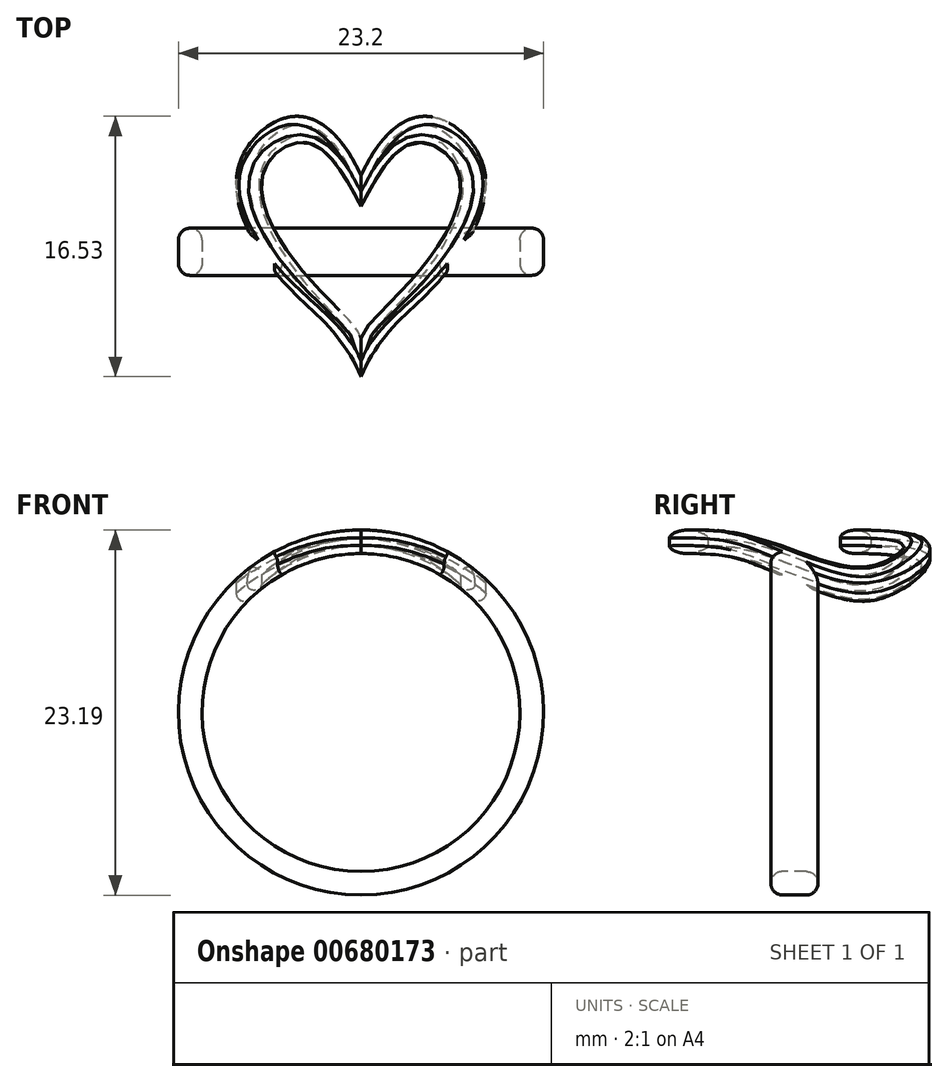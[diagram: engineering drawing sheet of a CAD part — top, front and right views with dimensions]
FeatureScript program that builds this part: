
annotation { "Feature Type Name" : "Feature", "Feature Type Description" : "" }
export const myFeature = defineFeature(function(context is Context, id is Id, definition is map)
    precondition{}
    {
        {
            var Q0;
            Q0=qCreatedBy(makeId("Top.planeOp"),FACE);
            var sketch = newSketch(context, id + "F0", { "sketchPlane" : qUnion([Q0])});
            skFitSpline(sketch, "E0", {"points": [v(0, 4.84) * mm, v(-4.43, 8.58) * mm, v(-7.87, 5.02) * mm, v(-5.4, -1.36) * mm, v(-1.9, -4.93) * mm, v(0, -7.93) * mm], "startDerivative": vector(-17.19, 37.33) * mm, "endDerivative": vector(6.53, -16.13) * mm});
            skFitSpline(sketch, "E1.MirrorCS", {"points": [v(0, 4.84) * mm, v(4.43, 8.58) * mm, v(7.87, 5.02) * mm, v(5.4, -1.36) * mm, v(1.9, -4.93) * mm, v(0, -7.93) * mm], "startDerivative": vector(17.19, 37.33) * mm, "endDerivative": vector(-6.53, -16.13) * mm});
            skSolve(sketch);
        }
        {
            var Q0;
            Q0 = qSketchRegion(id + "F0", true);
            extrude(context, id + "F1", {"entities" : qUnion([Q0]), "depth" : 19.05 * mm, "offsetDistance" : 25.4 * mm});
        }
        {
            var Q0;
            Q0=qCreatedBy(makeId("Front.planeOp"),FACE);
            var sketch = newSketch(context, id + "F2", { "sketchPlane" : qUnion([Q0])});
            skCircle(sketch, "E2", {"center": v(0, 0) * mm, "radius": 10.1 * mm});
            skCircle(sketch, "E3", {"center": v(0, 0) * mm, "radius": 11.6 * mm});
            skCircle(sketch, "E4", {"center": v(0, 0) * mm, "radius": 13.1 * mm});
            skCircle(sketch, "E5", {"center": v(0, 0) * mm, "radius": 23.1 * mm});
            skSolve(sketch);
        }
        {
            var Q0;
            Q0=makeQuery(id+"F2.imprint","IMPRINT",FACE,{"disambiguationData":[TD([[makeQuery(id+"F2.imprint","IMPRINT",EDGE,{"derivedFrom":sQuery(id+"F2.wireOp",EDGE,"E2")}),1.0]])]});
            extrude(context, id + "F3", {"entities" : qUnion([Q0]), "operationType" : NewBodyOperationType.REMOVE, "endBound" : BoundingType.SYMMETRIC, "oppositeDirection" : true, "depth" : 25.4 * mm, "offsetDistance" : 25.4 * mm});
        }
        {
            var Q0;
            Q0=makeQuery(id+"F2.imprint","IMPRINT",FACE,{"disambiguationData":[TD([[makeQuery(id+"F2.imprint","IMPRINT",EDGE,{"derivedFrom":sQuery(id+"F2.wireOp",EDGE,"E4")}),-1.0]])]});
            var Q1;
            Q1=makeQuery(id+"F2.imprint","IMPRINT",FACE,{"disambiguationData":[TD([[makeQuery(id+"F2.imprint","IMPRINT",EDGE,{"derivedFrom":sQuery(id+"F2.wireOp",EDGE,"E3")}),-1.0]])]});
            extrude(context, id + "F4", {"entities" : qUnion([Q0, Q1]), "operationType" : NewBodyOperationType.REMOVE, "endBound" : BoundingType.SYMMETRIC, "oppositeDirection" : true, "depth" : 25.4 * mm, "offsetDistance" : 25.4 * mm});
        }
        {
            var Q0;
            Q0=makeQuery(id+"F2.imprint","IMPRINT",FACE,{"disambiguationData":[TD([[makeQuery(id+"F2.imprint","IMPRINT",EDGE,{"derivedFrom":sQuery(id+"F2.wireOp",EDGE,"E2")}),-1.0]])]});
            extrude(context, id + "F5", {"entities" : qUnion([Q0]), "operationType" : NewBodyOperationType.ADD, "endBound" : BoundingType.SYMMETRIC, "oppositeDirection" : true, "depth" : 3 * mm, "offsetDistance" : 25.4 * mm});
        }
        {
            var Q0;
            Q0=qCreatedBy(makeId("Top.planeOp"),FACE);
            var sketch = newSketch(context, id + "F6", { "sketchPlane" : qUnion([Q0])});
            skFitSpline(sketch, "E6", {"points": [v(0, 2.9) * mm, v(-3.3, 6.9) * mm, v(-6.2, 5) * mm, v(-4.18, -0.63) * mm, v(-0.65, -4.45) * mm, v(0, -5.5) * mm], "startDerivative": vector(-11.42, 20.67) * mm, "endDerivative": vector(3.06, -10.59) * mm});
            skFitSpline(sketch, "E7.MirrorCS", {"points": [v(0, 2.9) * mm, v(3.3, 6.9) * mm, v(6.2, 5) * mm, v(4.18, -0.63) * mm, v(0.65, -4.45) * mm, v(0, -5.5) * mm], "startDerivative": vector(11.42, 20.67) * mm, "endDerivative": vector(-3.06, -10.59) * mm});
            skSolve(sketch);
        }
        {
            var Q0;
            Q0 = qSketchRegion(id + "F6", true);
            extrude(context, id + "F7", {"entities" : qUnion([Q0]), "operationType" : NewBodyOperationType.REMOVE, "depth" : 25.4 * mm, "offsetDistance" : 25.4 * mm});
        }
        {
            var Q0;
            Q0=makeQuery(id+"F5.opExtrude","CAP_EDGE",EDGE,{"disambiguationData":[OSD([sQuery(id+"F2.wireOp",EDGE,"E3")])],"isStart":false});
            var Q1;
            Q1=makeQuery(id+"F5.opExtrude","CAP_EDGE",EDGE,{"disambiguationData":[OSD([sQuery(id+"F2.wireOp",EDGE,"E3")])],"isStart":true});
            var Q2;
            Q2=makeQuery(id+"F5.opExtrude","CAP_EDGE",EDGE,{"disambiguationData":[OSD([sQuery(id+"F2.wireOp",EDGE,"E2")])],"isStart":true});
            var Q3;
            Q3=makeQuery(id+"F5.opExtrude","CAP_EDGE",EDGE,{"disambiguationData":[OSD([sQuery(id+"F2.wireOp",EDGE,"E2")])],"isStart":false});
            fillet(context, id + "F8", {"entities" : qUnion([Q0, Q1, Q2, Q3]), "radius" : 0.75 * mm, "tangentPropagation" : true, "allowEdgeOverflow" : false});
        }
        {
            var Q0;
            {var subQ0=sQuery(id+"F2.wireOp",EDGE,"E2");Q0=makeQuery(id+"F7.boolean.opBoolean","INTERSECT",EDGE,{"derivedFrom":[makeQuery(id+"F5.boolean.opBoolean","MERGE",FACE,{"derivedFrom":[makeQuery(id+"F3.boolean.opBoolean","COPY",FACE,{"derivedFrom":makeQuery(id+"F3.opExtrude","SWEPT_FACE",FACE,{"disambiguationData":[OSD([subQ0])]})}),makeQuery(id+"F5.opExtrude","SWEPT_FACE",FACE,{"disambiguationData":[OSD([subQ0])]})]}),makeQuery(id+"F7.opExtrude","SWEPT_FACE",FACE,{"disambiguationData":[OSD([sQuery(id+"F6.wireOp",EDGE,"E6")])]})]});}
            var Q1;
            {var subQ0=sQuery(id+"F2.wireOp",EDGE,"E3");Q1=makeQuery(id+"F7.boolean.opBoolean","INTERSECT",EDGE,{"derivedFrom":[makeQuery(id+"F5.boolean.opBoolean","MERGE",FACE,{"derivedFrom":[makeQuery(id+"F4.boolean.opBoolean","COPY",FACE,{"derivedFrom":makeQuery(id+"F4.opExtrude","SWEPT_FACE",FACE,{"disambiguationData":[OSD([subQ0])]})}),makeQuery(id+"F5.opExtrude","SWEPT_FACE",FACE,{"disambiguationData":[OSD([subQ0])]})]}),makeQuery(id+"F7.opExtrude","SWEPT_FACE",FACE,{"disambiguationData":[OSD([sQuery(id+"F6.wireOp",EDGE,"E7.MirrorCS")])]})]});}
            var Q2;
            {var subQ0=sQuery(id+"F2.wireOp",EDGE,"E2");Q2=makeQuery(id+"F7.boolean.opBoolean","INTERSECT",EDGE,{"derivedFrom":[makeQuery(id+"F5.boolean.opBoolean","MERGE",FACE,{"derivedFrom":[makeQuery(id+"F3.boolean.opBoolean","COPY",FACE,{"derivedFrom":makeQuery(id+"F3.opExtrude","SWEPT_FACE",FACE,{"disambiguationData":[OSD([subQ0])]})}),makeQuery(id+"F5.opExtrude","SWEPT_FACE",FACE,{"disambiguationData":[OSD([subQ0])]})]}),makeQuery(id+"F7.opExtrude","SWEPT_FACE",FACE,{"disambiguationData":[OSD([sQuery(id+"F6.wireOp",EDGE,"E7.MirrorCS")])]})]});}
            var Q3;
            {var subQ0=sQuery(id+"F2.wireOp",EDGE,"E3");Q3=makeQuery(id+"F7.boolean.opBoolean","INTERSECT",EDGE,{"derivedFrom":[makeQuery(id+"F5.boolean.opBoolean","MERGE",FACE,{"derivedFrom":[makeQuery(id+"F4.boolean.opBoolean","COPY",FACE,{"derivedFrom":makeQuery(id+"F4.opExtrude","SWEPT_FACE",FACE,{"disambiguationData":[OSD([subQ0])]})}),makeQuery(id+"F5.opExtrude","SWEPT_FACE",FACE,{"disambiguationData":[OSD([subQ0])]})]}),makeQuery(id+"F7.opExtrude","SWEPT_FACE",FACE,{"disambiguationData":[OSD([sQuery(id+"F6.wireOp",EDGE,"E6")])]})]});}
            var Q4;
            {var subQ0=sQuery(id+"F2.wireOp",EDGE,"E3");var subQ1=makeQuery(id+"F4.opExtrude","SWEPT_FACE",FACE,{"disambiguationData":[OSD([subQ0])]});var subQ2=makeQuery(id+"F1.opExtrude","SWEPT_FACE",FACE,{"disambiguationData":[OSD([sQuery(id+"F0.wireOp",EDGE,"E0")])]});Q4=makeQuery(id+"F5.boolean.opBoolean","SPLIT",EDGE,{"disambiguationData":[TD([makeQuery(id+"F5.opExtrude","CAP_FACE",FACE,{"disambiguationData":[OSD([sQuery(id+"F2.wireOp",EDGE,"E2"),subQ0])],"isStart":false})])],"derivedFrom":makeQuery(id+"F4.boolean.opBoolean","INTERSECT",EDGE,{"derivedFrom":[subQ2,subQ1]})});}
            var Q5;
            {var subQ0=sQuery(id+"F2.wireOp",EDGE,"E3");var subQ1=makeQuery(id+"F4.opExtrude","SWEPT_FACE",FACE,{"disambiguationData":[OSD([subQ0])]});var subQ2=makeQuery(id+"F1.opExtrude","SWEPT_FACE",FACE,{"disambiguationData":[OSD([sQuery(id+"F0.wireOp",EDGE,"E1.MirrorCS")])]});Q5=makeQuery(id+"F5.boolean.opBoolean","SPLIT",EDGE,{"disambiguationData":[TD([makeQuery(id+"F5.opExtrude","CAP_FACE",FACE,{"disambiguationData":[OSD([sQuery(id+"F2.wireOp",EDGE,"E2"),subQ0])],"isStart":false})])],"derivedFrom":makeQuery(id+"F4.boolean.opBoolean","INTERSECT",EDGE,{"derivedFrom":[subQ2,subQ1]})});}
            var Q6;
            {var subQ0=sQuery(id+"F2.wireOp",EDGE,"E3");var subQ1=makeQuery(id+"F4.opExtrude","SWEPT_FACE",FACE,{"disambiguationData":[OSD([subQ0])]});var subQ2=makeQuery(id+"F1.opExtrude","SWEPT_FACE",FACE,{"disambiguationData":[OSD([sQuery(id+"F0.wireOp",EDGE,"E1.MirrorCS")])]});Q6=makeQuery(id+"F5.boolean.opBoolean","SPLIT",EDGE,{"disambiguationData":[TD([makeQuery(id+"F5.opExtrude","CAP_FACE",FACE,{"disambiguationData":[OSD([sQuery(id+"F2.wireOp",EDGE,"E2"),subQ0])],"isStart":true})])],"derivedFrom":makeQuery(id+"F4.boolean.opBoolean","INTERSECT",EDGE,{"derivedFrom":[subQ2,subQ1]})});}
            var Q7;
            {var subQ0=sQuery(id+"F2.wireOp",EDGE,"E3");var subQ1=makeQuery(id+"F4.opExtrude","SWEPT_FACE",FACE,{"disambiguationData":[OSD([subQ0])]});var subQ2=makeQuery(id+"F1.opExtrude","SWEPT_FACE",FACE,{"disambiguationData":[OSD([sQuery(id+"F0.wireOp",EDGE,"E0")])]});Q7=makeQuery(id+"F5.boolean.opBoolean","SPLIT",EDGE,{"disambiguationData":[TD([makeQuery(id+"F5.opExtrude","CAP_FACE",FACE,{"disambiguationData":[OSD([sQuery(id+"F2.wireOp",EDGE,"E2"),subQ0])],"isStart":true})])],"derivedFrom":makeQuery(id+"F4.boolean.opBoolean","INTERSECT",EDGE,{"derivedFrom":[subQ2,subQ1]})});}
            var Q8;
            {var subQ0=sQuery(id+"F2.wireOp",EDGE,"E2");var subQ1=makeQuery(id+"F3.opExtrude","SWEPT_FACE",FACE,{"disambiguationData":[OSD([subQ0])]});var subQ2=makeQuery(id+"F1.opExtrude","SWEPT_FACE",FACE,{"disambiguationData":[OSD([sQuery(id+"F0.wireOp",EDGE,"E0")])]});Q8=makeQuery(id+"F5.boolean.opBoolean","SPLIT",EDGE,{"disambiguationData":[TD([makeQuery(id+"F5.opExtrude","CAP_FACE",FACE,{"disambiguationData":[OSD([subQ0,sQuery(id+"F2.wireOp",EDGE,"E3")])],"isStart":true})])],"derivedFrom":makeQuery(id+"F3.boolean.opBoolean","INTERSECT",EDGE,{"derivedFrom":[subQ2,subQ1]})});}
            var Q9;
            {var subQ0=sQuery(id+"F2.wireOp",EDGE,"E2");var subQ1=makeQuery(id+"F3.opExtrude","SWEPT_FACE",FACE,{"disambiguationData":[OSD([subQ0])]});var subQ2=makeQuery(id+"F1.opExtrude","SWEPT_FACE",FACE,{"disambiguationData":[OSD([sQuery(id+"F0.wireOp",EDGE,"E1.MirrorCS")])]});Q9=makeQuery(id+"F5.boolean.opBoolean","SPLIT",EDGE,{"disambiguationData":[TD([makeQuery(id+"F5.opExtrude","CAP_FACE",FACE,{"disambiguationData":[OSD([subQ0,sQuery(id+"F2.wireOp",EDGE,"E3")])],"isStart":true})])],"derivedFrom":makeQuery(id+"F3.boolean.opBoolean","INTERSECT",EDGE,{"derivedFrom":[subQ2,subQ1]})});}
            var Q10;
            {var subQ0=sQuery(id+"F2.wireOp",EDGE,"E2");var subQ1=makeQuery(id+"F3.opExtrude","SWEPT_FACE",FACE,{"disambiguationData":[OSD([subQ0])]});var subQ2=makeQuery(id+"F1.opExtrude","SWEPT_FACE",FACE,{"disambiguationData":[OSD([sQuery(id+"F0.wireOp",EDGE,"E0")])]});Q10=makeQuery(id+"F5.boolean.opBoolean","SPLIT",EDGE,{"disambiguationData":[TD([makeQuery(id+"F5.opExtrude","CAP_FACE",FACE,{"disambiguationData":[OSD([subQ0,sQuery(id+"F2.wireOp",EDGE,"E3")])],"isStart":false})])],"derivedFrom":makeQuery(id+"F3.boolean.opBoolean","INTERSECT",EDGE,{"derivedFrom":[subQ2,subQ1]})});}
            var Q11;
            {var subQ0=sQuery(id+"F2.wireOp",EDGE,"E2");var subQ1=makeQuery(id+"F3.opExtrude","SWEPT_FACE",FACE,{"disambiguationData":[OSD([subQ0])]});var subQ2=makeQuery(id+"F1.opExtrude","SWEPT_FACE",FACE,{"disambiguationData":[OSD([sQuery(id+"F0.wireOp",EDGE,"E1.MirrorCS")])]});Q11=makeQuery(id+"F5.boolean.opBoolean","SPLIT",EDGE,{"disambiguationData":[TD([makeQuery(id+"F5.opExtrude","CAP_FACE",FACE,{"disambiguationData":[OSD([subQ0,sQuery(id+"F2.wireOp",EDGE,"E3")])],"isStart":false})])],"derivedFrom":makeQuery(id+"F3.boolean.opBoolean","INTERSECT",EDGE,{"derivedFrom":[subQ2,subQ1]})});}
            fillet(context, id + "F9", {"entities" : qUnion([Q0, Q1, Q2, Q3, Q4, Q5, Q6, Q7, Q8, Q9, Q10, Q11]), "radius" : 0.5 * mm, "tangentPropagation" : true, "allowEdgeOverflow" : false});
        }
    });
